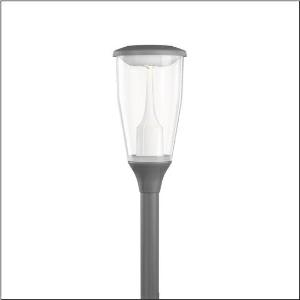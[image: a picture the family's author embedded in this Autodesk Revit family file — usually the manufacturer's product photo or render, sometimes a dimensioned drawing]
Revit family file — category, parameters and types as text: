
# Revit family: dl_11_iq___st1_2a_5xa5565kf14h000022_1156
name_source: partatom
category: Lighting Fixtures
units: mm (PartAtom-declared; Revit-internal decimal feet)

## family parameters
Cut with Voids When Loaded = No
Host = Face
Light Source = No
Part Type = Normal
Room Calculation Point = No
Round Connector Dimension = Use Diameter
Shared = No

## types (1)
- --- (1 x LED, 1560 lm, 10 W, 4000K)
    Apparent Load = 10 VA
    CIE Flux Codes = 24 63 94 96 100
    Color Rendering = 70
    Color Temperature = 4000K
    Default Elevation = 1800 mm
    Description = DL 11 iQ, mast luminaire, Module 540 iQ-SR, primary light control with 3 zone facetted reflector, of plastic, silver coated, highly specular, structured, primary optical cover: cover, of PMMA, transparent, light distribution: ST1.2a, light emission: direct distribution, primary light characteristic: asymmetric, installation type: post-top, LED, High Power LED, rated luminous flux: 1.560lm, luminous efficacy: 149lm/W, light colour: 740, colour temperature: 4000K, control: Street-Remote, Auto-Match, Temp-Guard, Lumen-Switch, Night-Set, Smart-Wire, Light-Fading, Desk-Remote (wireless, voltage-free reading and setting of iQ features in the workshop via application-optimized NFC function/RFID function), optimised constant luminous flux control (CLO 2.0), mains connection: 220..240V, AC, 50/60Hz, connection cable pre-assembled, cable length: 5,5m, start of lifetime: 10W, end of service life: 10W, reduction: 5W, luminaire housing, upper part, of diecast aluminium, coated, Siteco® metallic grey (DB 702S), spigot size: 60mm (post-top), post-top mast mounting element, of diecast aluminium, coated, Siteco® metallic grey (DB 702S), Module 540 iQ-SR, traffic white (RAL 9016), equipment: standard, protection rating (complete): IP66, insulation class (complete): insulation class II (safety insulation), certification: CE, ENEC, ENEC+, VDE, packaging unit: 1 piece

Light Distribution: ST1.2a
    Height = 665 mm
    Lamp = 1 x LED
    Lamp Light Flux = 1560 lm
    Lamp Power = 10 W
    Lamp count = 1
    Length = 334 mm
    Luminous efficacy = 156 lm/W
    Manufacturer = Siteco
    ModVariant = No
    Model = 5XA5565KF14H000022
    Number of Poles = 1
    OnlyDefault = Yes
    Power Factor = 1
    Product Name = DL 11 iQ | ST1.2a
    Product group = mast luminaire | pylon top
    ProductGroupID = 6100
    Protection Class = Protection class II
    Protection Degree = IP 66
    RLX_Detail_Level = 1
    RLX_Emergency_Light_Flux = 0 lm
    RLX_Emergency_Type = 0
    RLX_Emergency_Type_DB = No
    RlxData = <blob elided: 155949 chars, md5=3bb86049>
    Socket = socket
    Standby Power = 0 W
    System Light Flux = 1560 lm
    System Power = 10 W
    Type Comments = factory setting: luminous flux: 100 % | dim-lin: 254 | 401 mA
    Type Image = l_1258354.jpg
    URL = http://relux.com
    VarID = @adj_044029
    Voltage = 0 V
    Weight = 0.00 kg
    Width = 0 mm  [stored 0 ft]

note: [stored X ft] marks values corroborated as IEEE doubles in the binary element streams (Revit-internal decimal feet)

## geometry (parser evidence)
native form markers: Blend x4, Sweep x9
no freeform markers — native parametric forms only
